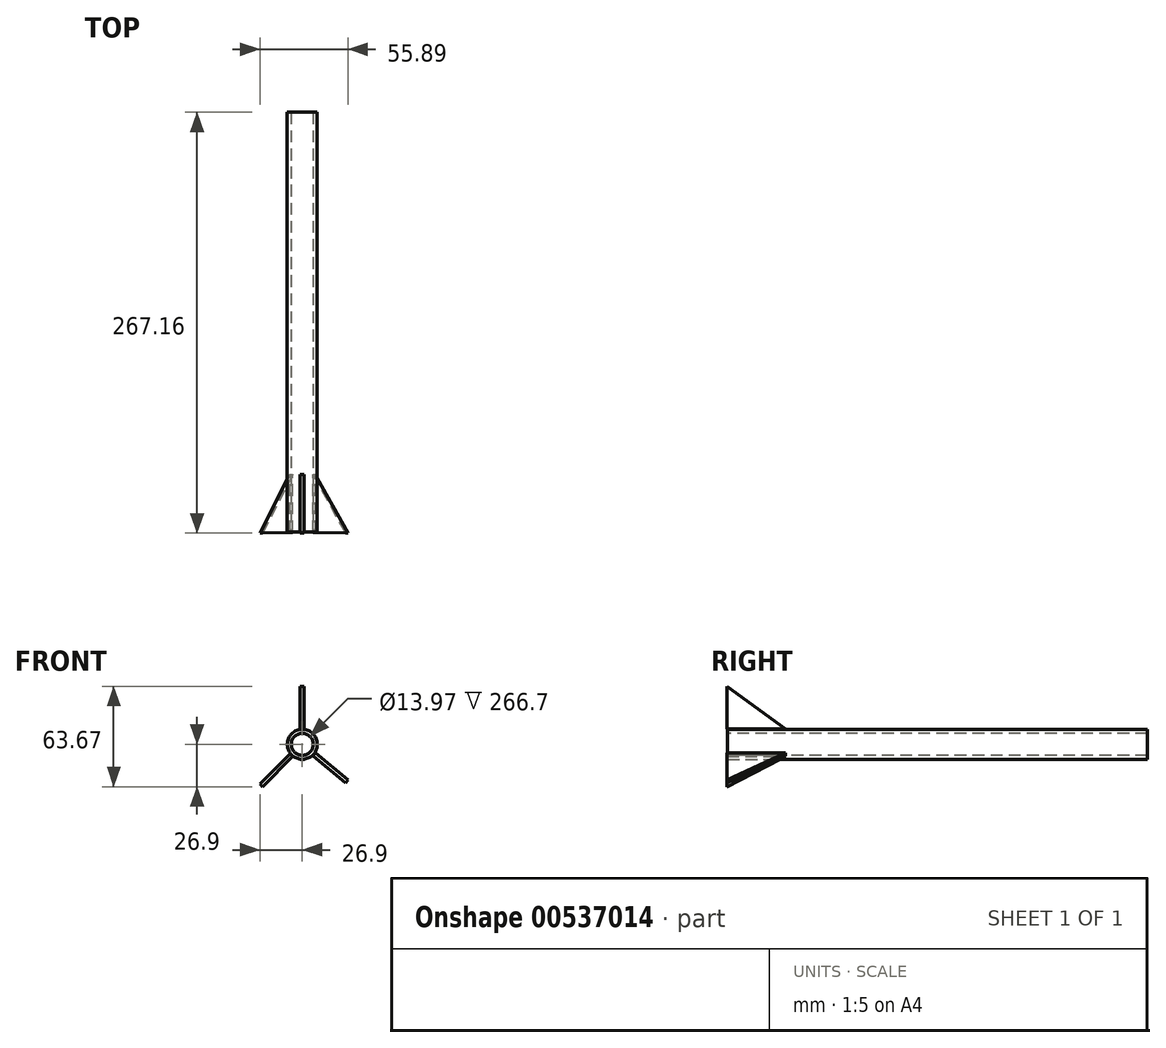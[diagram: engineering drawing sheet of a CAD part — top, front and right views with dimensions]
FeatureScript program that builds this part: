
annotation { "Feature Type Name" : "Feature", "Feature Type Description" : "" }
export const myFeature = defineFeature(function(context is Context, id is Id, definition is map)
    precondition{}
    {
        {
            var Q0;
            Q0=qCreatedBy(makeId("Front.planeOp"),FACE);
            var sketch = newSketch(context, id + "F0", { "sketchPlane" : qUnion([Q0])});
            skCircle(sketch, "E0", {"center": v(0, 0) * mm, "radius": 9.53 * mm});
            skSolve(sketch);
        }
        {
            var Q0;
            Q0 = qSketchRegion(id + "F0", true);
            extrude(context, id + "F1", {"entities" : qUnion([Q0]), "endBound" : BoundingType.SYMMETRIC, "depth" : 266.7 * mm, "offsetDistance" : 25.4 * mm});
        }
        {
            var Q0;
            Q0=qCreatedBy(makeId("Front.planeOp"),FACE);
            var sketch = newSketch(context, id + "F2", { "sketchPlane" : qUnion([Q0])});
            skCircle(sketch, "E1", {"center": v(0, 0) * mm, "radius": 6.99 * mm});
            skSolve(sketch);
        }
        {
            var Q0;
            Q0 = qSketchRegion(id + "F2", true);
            extrude(context, id + "F3", {"entities" : qUnion([Q0]), "operationType" : NewBodyOperationType.REMOVE, "endBound" : BoundingType.SYMMETRIC, "oppositeDirection" : true, "depth" : 266.7 * mm, "offsetDistance" : 25.4 * mm});
        }
        {
            var Q0;
            Q0=qCreatedBy(makeId("Right.planeOp"),FACE);
            var sketch = newSketch(context, id + "F4", { "sketchPlane" : qUnion([Q0])});
            skLineSegment(sketch, "E2", {"start": v(-133.55, 9.79) * mm, "end": v(-96.6, 9.79) * mm});
            skLineSegment(sketch, "E3", {"start": v(-96.6, 9.79) * mm, "end": v(-133.8, 36.77) * mm});
            skLineSegment(sketch, "E4", {"start": v(-133.8, 36.77) * mm, "end": v(-133.55, 9.79) * mm});
            skSolve(sketch);
        }
        {
            var Q0;
            Q0 = qSketchRegion(id + "F4", true);
            extrude(context, id + "F5", {"entities" : qUnion([Q0]), "endBound" : BoundingType.SYMMETRIC, "depth" : 2.54 * mm, "offsetDistance" : 25.4 * mm});
        }
        {
            var Q0;
            Q0=makeQuery(id+"F5.opExtrude","SWEPT_BODY",BODY,{"disambiguationData":[OSD([sQuery(id+"F4.wireOp",EDGE,"E2"),sQuery(id+"F4.wireOp",EDGE,"E3"),sQuery(id+"F4.wireOp",EDGE,"E4")])]});
            var Q1;
            Q1=makeQuery(id+"F1.opExtrude","CAP_EDGE",EDGE,{"disambiguationData":[OSD([sQuery(id+"F0.wireOp",EDGE,"E0")])],"isStart":false});
            transform(context, id + "F6", {"entities" : qUnion([Q0]), "transformType" : TransformType.ROTATION, "transformAxis" : qUnion([Q1]), "angle" : 135 * degree, "makeCopy" : true});
        }
        {
            var Q0;
            Q0=makeQuery(id+"F6.opPattern","COPY",BODY,{"derivedFrom":makeQuery(id+"F5.opExtrude","SWEPT_BODY",BODY,{"disambiguationData":[OSD([sQuery(id+"F4.wireOp",EDGE,"E2"),sQuery(id+"F4.wireOp",EDGE,"E3"),sQuery(id+"F4.wireOp",EDGE,"E4")])]}),"instanceName":"1"});
            var Q1;
            Q1=makeQuery(id+"F1.opExtrude","CAP_EDGE",EDGE,{"disambiguationData":[OSD([sQuery(id+"F0.wireOp",EDGE,"E0")])],"isStart":false});
            transform(context, id + "F7", {"entities" : qUnion([Q0]), "transformType" : TransformType.ROTATION, "transformAxis" : qUnion([Q1]), "angle" : 95 * degree, "makeCopy" : true});
        }
    });
